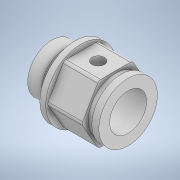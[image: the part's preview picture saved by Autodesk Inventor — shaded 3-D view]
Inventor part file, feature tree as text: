
AUTODESK INVENTOR PART (.ipt)
format: ipt  version: 2020 (Build 240168000, 168)  size: 387,584 bytes
history: native  units: mm
features: sketch x10, extrude x8, fillet x3
ambient origin geometry x8: Origin, YZ Plane, XZ Plane, XY Plane, X Axis, Y Axis, Z Axis, Center Point
bodies: Solid1 (feature_tree)
feature tree (21):
  extrude  "Extrusion1"  Depth=1.28mm TaperAngle=0.0deg
  extrude  "Extrusion2"  Depth=11.854mm
  extrude  "Extrusion3"  Depth=1.5mm TaperAngle=0.0deg
  extrude  "Extrusion4"  Depth=0.75mm
  fillet  "Fillet1"  Radius=2.705mm
  fillet  "Fillet2"  Radius=6.5mm
  sketch  "Sketch5"  dims[d15=6.4mm d16=11.75mm d17=0.0mm]
  extrude  "Extrusion5"  Depth=11.75mm TaperAngle=0.0deg
  sketch  "Sketch7"  dims[d21=10.5mm d22=5.0mm d23=0.0mm]
  sketch  "Sketch8"  dims[d24=2.0mm]
  extrude  "Extrusion6"  Depth=13.75mm TaperAngle=0.0deg
  extrude  "Extrusion7"  Depth=5.0mm TaperAngle=0.0deg
  extrude  "Extrusion8"  [1 undecoded]
  fillet  "Fillet3"  [1 undecoded]
  sketch  "Sketch1"  dims[d0=15.197mm d1=1.28mm d2=0.0mm]
  sketch  "Sketch2"  dims[d3=7.5mm d4=0.0mm d5=11.854mm]
  sketch  "Sketch3"  dims[d6=1.22mm d7=0.0mm d8=1.5mm d9=0.0mm]
  sketch  "Sketch4"  dims[d10=0.75mm d11=0.75mm d12=2.705mm d13=6.5mm d14=0.0mm]
  sketch  "Sketch6"  dims[d18=8.0mm d19=13.75mm d20=0.0mm]
  sketch  "Sketch9"
  sketch  "Sketch10"
note: 2 required parameter values undecoded (feature->parameter linkage not recoverable at this tier; creation-order binding heuristic only, values carry confidence <= 0.55)
